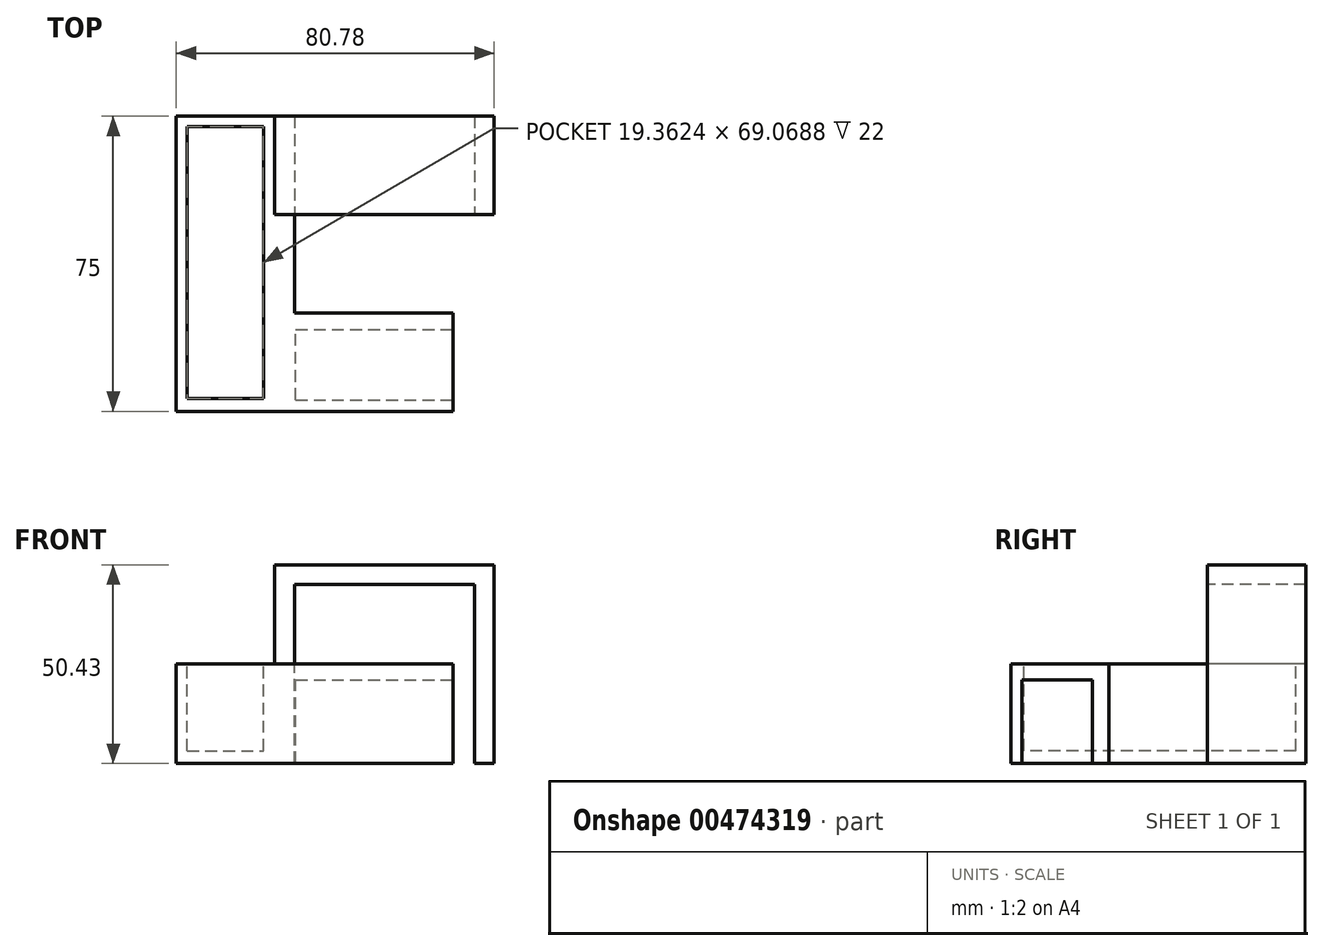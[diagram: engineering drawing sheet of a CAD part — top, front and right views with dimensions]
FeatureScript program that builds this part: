
annotation { "Feature Type Name" : "Feature", "Feature Type Description" : "" }
export const myFeature = defineFeature(function(context is Context, id is Id, definition is map)
    precondition{}
    {
        {
            var Q0;
            Q0=qCreatedBy(makeId("Front.planeOp"),FACE);
            var sketch = newSketch(context, id + "F0", { "sketchPlane" : qUnion([Q0])});
            skLineSegment(sketch, "E0.bottom", {"start": v(0, 0) * mm, "end": v(55.78, 0) * mm});
            skLineSegment(sketch, "E0.top", {"start": v(0, 50.43) * mm, "end": v(55.78, 50.43) * mm});
            skLineSegment(sketch, "E0.left", {"start": v(0, 0) * mm, "end": v(0, 50.43) * mm});
            skLineSegment(sketch, "E0.right", {"start": v(55.78, 0) * mm, "end": v(55.78, 50.43) * mm});
            skLineSegment(sketch, "E1.0", {"start": v(50.78, 0) * mm, "end": v(50.78, 45.43) * mm});
            skLineSegment(sketch, "E1.1", {"start": v(5, 45.43) * mm, "end": v(50.78, 45.43) * mm});
            skLineSegment(sketch, "E1.2", {"start": v(5, 0) * mm, "end": v(5, 45.43) * mm});
            skLineSegment(sketch, "E2", {"start": v(0, 25.21) * mm, "end": v(5, 25.21) * mm});
            skSolve(sketch);
        }
        {
            var Q0;
            {var subQ2=sQuery(id+"F0.wireOp",EDGE,"E0.top");Q0=makeQuery(id+"F0.imprint","IMPRINT",FACE,{"disambiguationData":[TD([[makeQuery(id+"F0.imprint","IMPRINT",EDGE,{"derivedFrom":subQ2}),-1.0]])]});}
            var Q1;
            {var subQ5=sQuery(id+"F0.wireOp",EDGE,"E2");Q1=makeQuery(id+"F0.imprint","IMPRINT",FACE,{"disambiguationData":[TD([[makeQuery(id+"F0.imprint","IMPRINT",EDGE,{"derivedFrom":subQ5}),-1.0]])]});}
            extrude(context, id + "F1", {"entities" : qUnion([Q0, Q1]), "oppositeDirection" : true, "depth" : 25 * mm});
        }
        {
            var Q0;
            {var subQ5=sQuery(id+"F0.wireOp",EDGE,"E2");Q0=makeQuery(id+"F0.imprint","IMPRINT",FACE,{"disambiguationData":[TD([[makeQuery(id+"F0.imprint","IMPRINT",EDGE,{"derivedFrom":subQ5}),-1.0]])]});}
            extrude(context, id + "F2", {"entities" : qUnion([Q0]), "operationType" : NewBodyOperationType.ADD, "depth" : 25 * mm});
        }
        {
            var Q0;
            Q0=makeQuery(id+"F2.opExtrude","CAP_FACE",FACE,{"disambiguationData":[OSD([sQuery(id+"F0.wireOp",EDGE,"E0.bottom"),sQuery(id+"F0.wireOp",EDGE,"E0.left"),sQuery(id+"F0.wireOp",EDGE,"E1.2"),sQuery(id+"F0.wireOp",EDGE,"E2")])],"isStart":false});
            var sketch = newSketch(context, id + "F3", { "sketchPlane" : qUnion([Q0])});
            skLineSegment(sketch, "E3.bottom", {"start": v(0, 0) * mm, "end": v(45.35, 0) * mm});
            skLineSegment(sketch, "E3.top", {"start": v(0, 25.21) * mm, "end": v(45.35, 25.21) * mm});
            skLineSegment(sketch, "E3.left", {"start": v(0, 0) * mm, "end": v(0, 25.21) * mm});
            skLineSegment(sketch, "E3.right", {"start": v(45.35, 0) * mm, "end": v(45.35, 25.21) * mm});
            skSolve(sketch);
        }
        {
            var Q0;
            {var subQ2=sQuery(id+"F3.wireOp",EDGE,"E3.right");Q0=makeQuery(id+"F3.imprint","IMPRINT",FACE,{"disambiguationData":[TD([[makeQuery(id+"F3.imprint","IMPRINT",EDGE,{"derivedFrom":subQ2}),1.0]])]});}
            var Q1;
            {var subQ0=sQuery(id+"F3.wireOp",EDGE,"E3.left");Q1=makeQuery(id+"F3.imprint","IMPRINT",FACE,{"disambiguationData":[TD([[makeQuery(id+"F3.imprint","IMPRINT",EDGE,{"derivedFrom":subQ0}),-1.0]])]});}
            extrude(context, id + "F4", {"entities" : qUnion([Q0, Q1]), "operationType" : NewBodyOperationType.ADD, "depth" : 25 * mm});
        }
        {
            var Q0;
            {var subQ0=sQuery(id+"F0.wireOp",EDGE,"E0.left");Q0=makeQuery(id+"F4.boolean.opBoolean","MERGE",FACE,{"derivedFrom":[makeQuery(id+"F2.boolean.opBoolean","MERGE",FACE,{"derivedFrom":[makeQuery(id+"F1.opExtrude","SWEPT_FACE",FACE,{"disambiguationData":[OSD([subQ0])]}),makeQuery(id+"F2.opExtrude","SWEPT_FACE",FACE,{"disambiguationData":[OSD([subQ0])]})]}),makeQuery(id+"F4.opExtrude","SWEPT_FACE",FACE,{"disambiguationData":[OSD([sQuery(id+"F3.wireOp",EDGE,"E3.left")])]})]});}
            var sketch = newSketch(context, id + "F5", { "sketchPlane" : qUnion([Q0])});
            skLineSegment(sketch, "E4.bottom", {"start": v(-25, 0) * mm, "end": v(50, 0) * mm});
            skLineSegment(sketch, "E4.top", {"start": v(-25, 25.21) * mm, "end": v(50, 25.21) * mm});
            skLineSegment(sketch, "E4.left", {"start": v(-25, 0) * mm, "end": v(-25, 25.21) * mm});
            skLineSegment(sketch, "E4.right", {"start": v(50, 0) * mm, "end": v(50, 25.21) * mm});
            skSolve(sketch);
        }
        {
            var Q0;
            Q0=makeQuery(id+"F5.imprint","IMPRINT",FACE,{"disambiguationData":[TD([[makeQuery(id+"F5.imprint","IMPRINT",EDGE,{"derivedFrom":sQuery(id+"F5.wireOp",EDGE,"E4.bottom")}),1.0]])]});
            extrude(context, id + "F6", {"entities" : qUnion([Q0]), "operationType" : NewBodyOperationType.ADD, "depth" : 25 * mm});
        }
        {
            var Q0;
            Q0=makeQuery(id+"F6.boolean.opBoolean","MERGE",FACE,{"derivedFrom":[makeQuery(id+"F4.boolean.opBoolean","MERGE",FACE,{"derivedFrom":[makeQuery(id+"F2.opExtrude","SWEPT_FACE",FACE,{"disambiguationData":[OSD([sQuery(id+"F0.wireOp",EDGE,"E2")])]}),makeQuery(id+"F4.opExtrude","SWEPT_FACE",FACE,{"disambiguationData":[OSD([sQuery(id+"F3.wireOp",EDGE,"E3.top")])]})]}),makeQuery(id+"F6.opExtrude","SWEPT_FACE",FACE,{"disambiguationData":[OSD([sQuery(id+"F5.wireOp",EDGE,"E4.top")])]})]});
            var sketch = newSketch(context, id + "F7", { "sketchPlane" : qUnion([Q0])});
            skLineSegment(sketch, "E5.bottom", {"start": v(-22.25, 22.4) * mm, "end": v(-2.89, 22.4) * mm});
            skLineSegment(sketch, "E5.top", {"start": v(-22.25, -46.67) * mm, "end": v(-2.89, -46.67) * mm});
            skLineSegment(sketch, "E5.left", {"start": v(-22.25, 22.4) * mm, "end": v(-22.25, -46.67) * mm});
            skLineSegment(sketch, "E5.right", {"start": v(-2.89, 22.4) * mm, "end": v(-2.89, -46.67) * mm});
            skSolve(sketch);
        }
        {
            var Q0;
            Q0=makeQuery(id+"F7.imprint","IMPRINT",FACE,{"disambiguationData":[TD([[makeQuery(id+"F7.imprint","IMPRINT",EDGE,{"derivedFrom":sQuery(id+"F7.wireOp",EDGE,"E5.bottom")}),-1.0]])]});
            extrude(context, id + "F8", {"entities" : qUnion([Q0]), "operationType" : NewBodyOperationType.REMOVE, "oppositeDirection" : true, "depth" : 22 * mm});
        }
        {
            var Q0;
            Q0=makeQuery(id+"F4.opExtrude","SWEPT_FACE",FACE,{"disambiguationData":[OSD([sQuery(id+"F3.wireOp",EDGE,"E3.right")])]});
            var sketch = newSketch(context, id + "F9", { "sketchPlane" : qUnion([Q0])});
            skLineSegment(sketch, "E6.bottom", {"start": v(-47.1, 0) * mm, "end": v(-29.19, 0) * mm});
            skLineSegment(sketch, "E6.top", {"start": v(-47.1, 21.24) * mm, "end": v(-29.19, 21.24) * mm});
            skLineSegment(sketch, "E6.left", {"start": v(-47.1, 0) * mm, "end": v(-47.1, 21.24) * mm});
            skLineSegment(sketch, "E6.right", {"start": v(-29.19, 0) * mm, "end": v(-29.19, 21.24) * mm});
            skSolve(sketch);
        }
        {
            var Q0;
            Q0=makeQuery(id+"F9.imprint","IMPRINT",FACE,{"disambiguationData":[TD([[makeQuery(id+"F9.imprint","IMPRINT",EDGE,{"derivedFrom":sQuery(id+"F9.wireOp",EDGE,"E6.bottom")}),1.0]])]});
            extrude(context, id + "F10", {"entities" : qUnion([Q0]), "operationType" : NewBodyOperationType.REMOVE, "oppositeDirection" : true, "depth" : 40 * mm});
        }
    });
